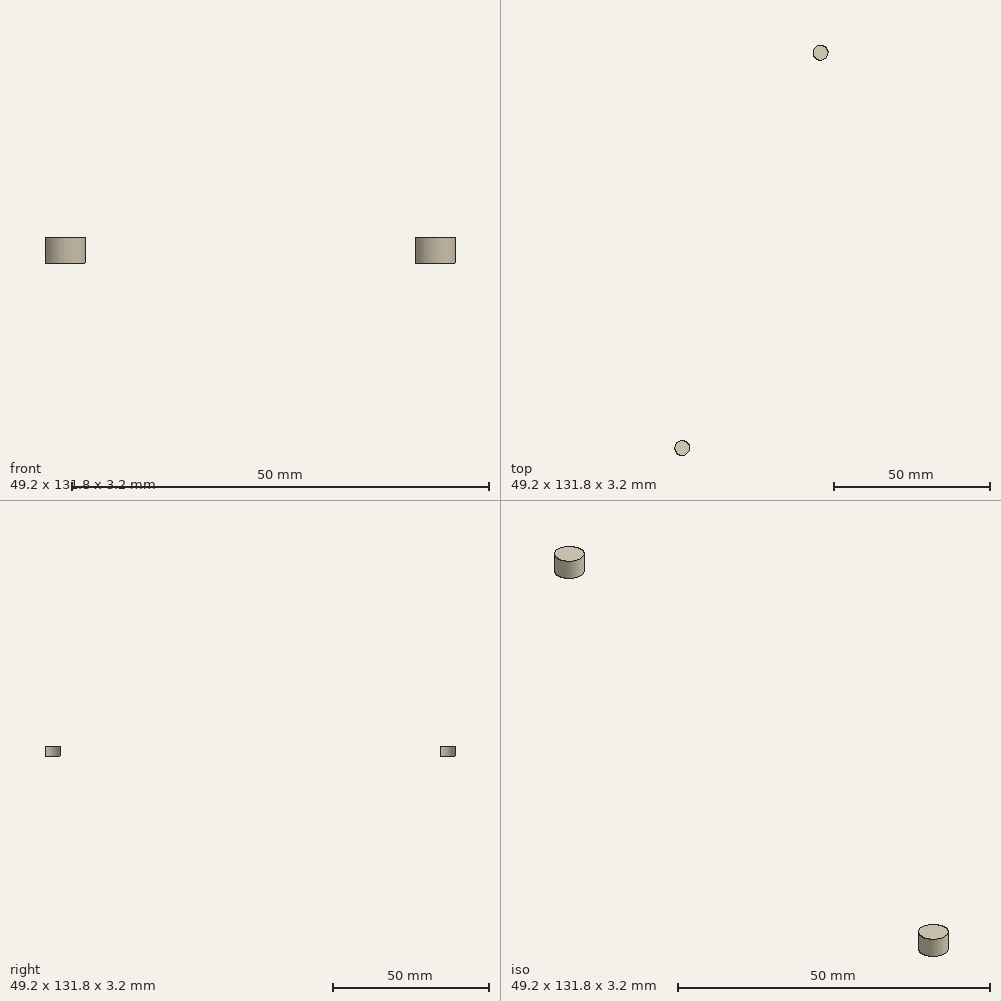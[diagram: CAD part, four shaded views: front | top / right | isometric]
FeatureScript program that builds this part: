
annotation { "Feature Type Name" : "Feature", "Feature Type Description" : "" }
export const myFeature = defineFeature(function(context is Context, id is Id, definition is map)
    precondition{}
    {
        {
            var Q0;
            Q0=qCreatedBy(makeId("Top.planeOp"),FACE);
            var sketch = newSketch(context, id + "F0", { "sketchPlane" : qUnion([Q0])});
            skLineSegment(sketch, "E0.rect.bottom", {"start": v(28.58, 69.85) * mm, "end": v(-28.57, 69.85) * mm});
            skLineSegment(sketch, "E0.rect.top", {"start": v(28.57, -69.85) * mm, "end": v(-28.58, -69.85) * mm});
            skLineSegment(sketch, "E0.rect.left", {"start": v(28.58, 69.85) * mm, "end": v(28.57, -69.85) * mm});
            skLineSegment(sketch, "E0.rect.right", {"start": v(-28.57, 69.85) * mm, "end": v(-28.58, -69.85) * mm});
            skPoint(sketch, "E0.rect.middle", {"position": v(0, 0) * mm});
            skSolve(sketch);
        }
        {
            var Q0;
            Q0=makeQuery(id+"F0.imprint","IMPRINT",FACE,{"disambiguationData":[TD([[makeQuery(id+"F0.imprint","IMPRINT",EDGE,{"derivedFrom":sQuery(id+"F0.wireOp",EDGE,"E0.rect.bottom")}),1.0]])]});
            extrude(context, id + "F1", {"entities" : qUnion([Q0]), "endBound" : BoundingType.SYMMETRIC, "depth" : 3.17 * mm});
        }
        {
            var Q0;
            Q0=makeQuery(id+"F1.opExtrude","CAP_FACE",FACE,{"disambiguationData":[OSD([sQuery(id+"F0.wireOp",EDGE,"E0.rect.bottom"),sQuery(id+"F0.wireOp",EDGE,"E0.rect.top"),sQuery(id+"F0.wireOp",EDGE,"E0.rect.left"),sQuery(id+"F0.wireOp",EDGE,"E0.rect.right")])],"isStart":false});
            var sketch = newSketch(context, id + "F2", { "sketchPlane" : qUnion([Q0])});
            skLineSegment(sketch, "E1", {"start": v(28.57, -69.85) * mm, "end": v(22.22, -69.85) * mm, "construction": true});
            skLineSegment(sketch, "E2", {"start": v(22.22, -69.85) * mm, "end": v(22.22, -63.5) * mm, "construction": true});
            skCircle(sketch, "E3", {"center": v(22.22, -63.5) * mm, "radius": 2.38 * mm});
            skCircle(sketch, "E4.MirrorC", {"center": v(-22.22, -63.5) * mm, "radius": 2.38 * mm});
            skCircle(sketch, "E5.MirrorC", {"center": v(-22.22, 63.5) * mm, "radius": 2.38 * mm});
            skCircle(sketch, "E6.MirrorC", {"center": v(22.22, 63.5) * mm, "radius": 2.38 * mm});
            skSolve(sketch);
        }
        {
            var Q0;
            Q0=makeQuery(id+"F2.imprint","IMPRINT",FACE,{"disambiguationData":[TD([[makeQuery(id+"F2.imprint","IMPRINT",EDGE,{"derivedFrom":sQuery(id+"F2.wireOp",EDGE,"E5.MirrorC")}),1.0]])]});
            var Q1;
            Q1=makeQuery(id+"F2.imprint","IMPRINT",FACE,{"disambiguationData":[TD([[makeQuery(id+"F2.imprint","IMPRINT",EDGE,{"derivedFrom":sQuery(id+"F2.wireOp",EDGE,"E6.MirrorC")}),-1.0]])]});
            var Q2;
            Q2=makeQuery(id+"F2.imprint","IMPRINT",FACE,{"disambiguationData":[TD([[makeQuery(id+"F2.imprint","IMPRINT",EDGE,{"derivedFrom":sQuery(id+"F2.wireOp",EDGE,"E4.MirrorC")}),-1.0]])]});
            var Q3;
            Q3=makeQuery(id+"F2.imprint","IMPRINT",FACE,{"disambiguationData":[TD([[makeQuery(id+"F2.imprint","IMPRINT",EDGE,{"derivedFrom":sQuery(id+"F2.wireOp",EDGE,"E3")}),1.0]])]});
            extrude(context, id + "F3", {"entities" : qUnion([Q0, Q1, Q2, Q3]), "operationType" : NewBodyOperationType.REMOVE, "endBound" : BoundingType.UP_TO_NEXT, "oppositeDirection" : true, "depth" : 25.4 * mm});
        }
    });
